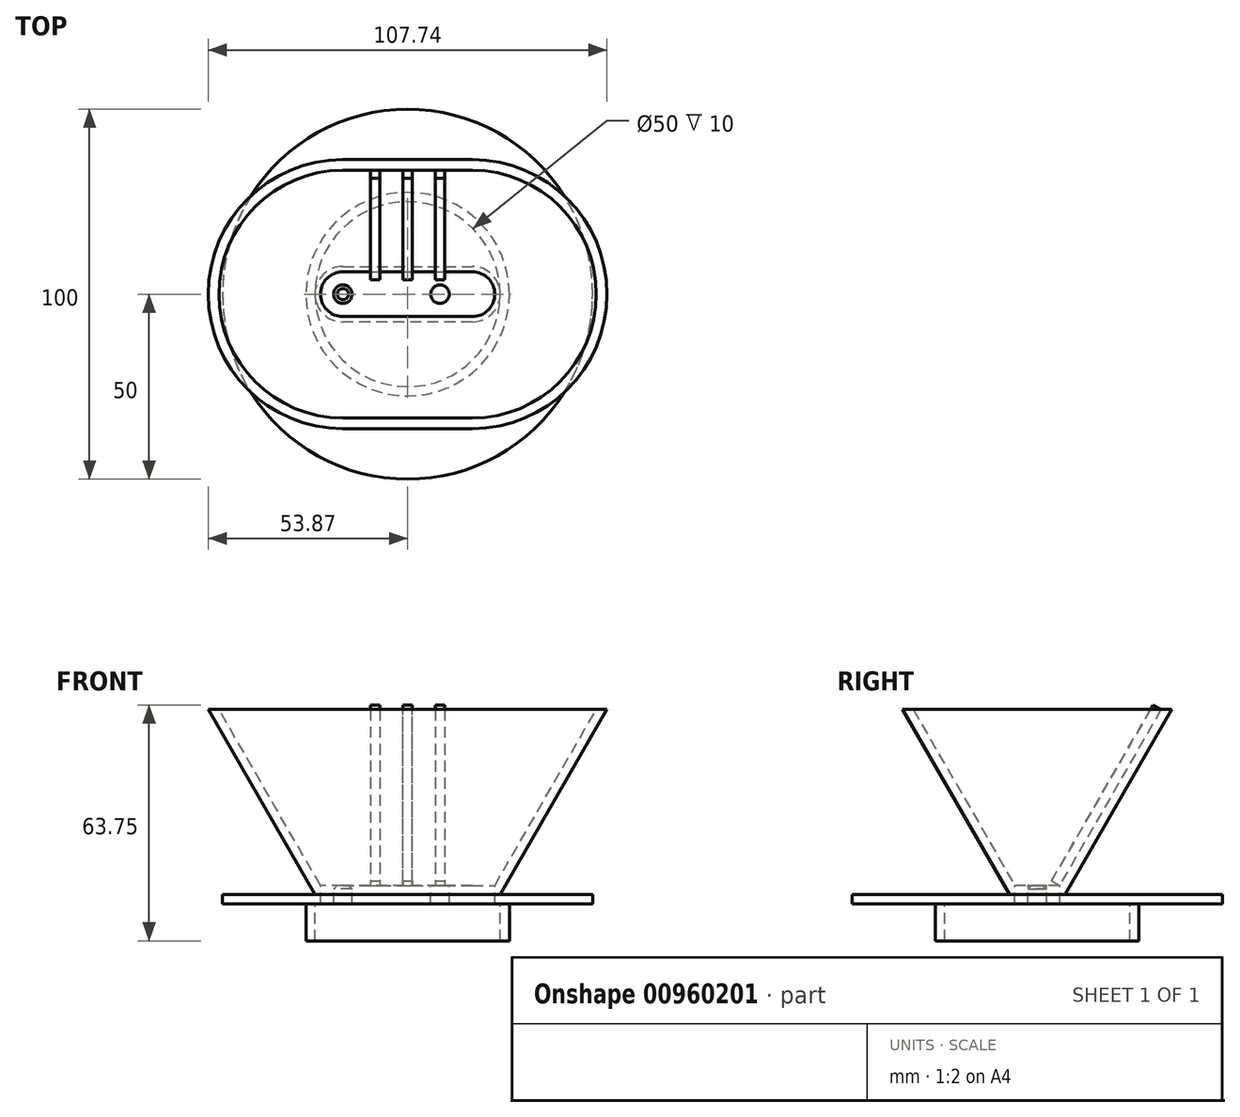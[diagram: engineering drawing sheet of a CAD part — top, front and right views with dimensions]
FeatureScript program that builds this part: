
annotation { "Feature Type Name" : "Feature", "Feature Type Description" : "" }
export const myFeature = defineFeature(function(context is Context, id is Id, definition is map)
    precondition{}
    {
        {
            var Q0;
            Q0=qCreatedBy(makeId("Top.planeOp"),FACE);
            var sketch = newSketch(context, id + "F0", { "sketchPlane" : qUnion([Q0])});
            skLineSegment(sketch, "E0.bottom", {"start": v(17.5, 7.5) * mm, "end": v(-17.5, 7.5) * mm});
            skLineSegment(sketch, "E0.top", {"start": v(17.5, -7.5) * mm, "end": v(-17.5, -7.5) * mm});
            skLineSegment(sketch, "E0.left", {"start": v(25, 0) * mm, "end": v(25, 0) * mm});
            skLineSegment(sketch, "E0.right", {"start": v(-25, 0) * mm, "end": v(-25, 0) * mm});
            skPoint(sketch, "E0.middle", {"position": v(0, 0) * mm});
            skPoint(sketch, "E1.visualSharp", {"position": v(-25, 7.5) * mm});
            skArc(sketch, "E1.filletArc", {"start": v(-17.5, 7.5) * mm, "mid": v(-22.8, 5.3) * mm, "end": v(-25, 0) * mm});
            skPoint(sketch, "E2.visualSharp", {"position": v(-25, -7.5) * mm});
            skArc(sketch, "E2.filletArc", {"start": v(-25, 0) * mm, "mid": v(-22.8, -5.3) * mm, "end": v(-17.5, -7.5) * mm});
            skPoint(sketch, "E3.visualSharp", {"position": v(25, -7.5) * mm});
            skArc(sketch, "E3.filletArc", {"start": v(17.5, -7.5) * mm, "mid": v(22.8, -5.3) * mm, "end": v(25, 0) * mm});
            skPoint(sketch, "E4.visualSharp", {"position": v(25, 7.5) * mm});
            skArc(sketch, "E4.filletArc", {"start": v(25, 0) * mm, "mid": v(22.8, 5.3) * mm, "end": v(17.5, 7.5) * mm});
            skSolve(sketch);
        }
        {
            var Q0;
            Q0=makeQuery(id+"F0.imprint","IMPRINT",FACE,{"disambiguationData":[TD([[makeQuery(id+"F0.imprint","IMPRINT",EDGE,{"derivedFrom":sQuery(id+"F0.wireOp",EDGE,"E0.bottom")}),1.0]])]});
            extrude(context, id + "F1", {"entities" : qUnion([Q0]), "depth" : 50 * mm, "offsetDistance" : 25 * mm, "hasDraft" : true, "draftAngle" : 30 * degree});
        }
        {
            var Q0;
            Q0=makeQuery(id+"F1.opExtrude","CAP_FACE",FACE,{"disambiguationData":[OSD([sQuery(id+"F0.wireOp",EDGE,"E0.bottom"),sQuery(id+"F0.wireOp",EDGE,"E0.top"),sQuery(id+"F0.wireOp",EDGE,"E0.left"),sQuery(id+"F0.wireOp",EDGE,"E0.right"),sQuery(id+"F0.wireOp",EDGE,"E1.filletArc"),sQuery(id+"F0.wireOp",EDGE,"E2.filletArc"),sQuery(id+"F0.wireOp",EDGE,"E3.filletArc"),sQuery(id+"F0.wireOp",EDGE,"E4.filletArc")])],"isStart":false});
            shell(context, id + "F2", {"entities" : qUnion([Q0]), "thickness" : 2.5 * mm});
        }
        {
            var Q0;
            Q0=makeQuery(id+"F1.opExtrude","CAP_FACE",FACE,{"disambiguationData":[OSD([sQuery(id+"F0.wireOp",EDGE,"E0.bottom"),sQuery(id+"F0.wireOp",EDGE,"E0.top"),sQuery(id+"F0.wireOp",EDGE,"E1.filletArc"),sQuery(id+"F0.wireOp",EDGE,"E2.filletArc"),sQuery(id+"F0.wireOp",EDGE,"E3.filletArc"),sQuery(id+"F0.wireOp",EDGE,"E4.filletArc")])],"isStart":true});
            var sketch = newSketch(context, id + "F3", { "sketchPlane" : qUnion([Q0])});
            skCircle(sketch, "E5", {"center": v(0, 0) * mm, "radius": 50 * mm});
            skSolve(sketch);
        }
        {
            var Q0;
            Q0 = qSketchRegion(id + "F3", true);
            extrude(context, id + "F4", {"entities" : qUnion([Q0]), "operationType" : NewBodyOperationType.ADD, "depth" : 2.5 * mm, "offsetDistance" : 25 * mm});
        }
        {
            var Q0;
            Q0=makeQuery(id+"F4.opExtrude","CAP_FACE",FACE,{"disambiguationData":[OSD([sQuery(id+"F3.wireOp",EDGE,"E5")])],"isStart":false});
            var sketch = newSketch(context, id + "F5", { "sketchPlane" : qUnion([Q0])});
            skCircle(sketch, "E6", {"center": v(0, 0) * mm, "radius": 25 * mm});
            skCircle(sketch, "E7", {"center": v(0, 0) * mm, "radius": 27.5 * mm});
            skSolve(sketch);
        }
        {
            var Q0;
            Q0=makeQuery(id+"F5.imprint","IMPRINT",FACE,{"disambiguationData":[TD([[makeQuery(id+"F5.imprint","IMPRINT",EDGE,{"derivedFrom":sQuery(id+"F5.wireOp",EDGE,"E6")}),-1.0]])]});
            extrude(context, id + "F6", {"entities" : qUnion([Q0]), "operationType" : NewBodyOperationType.ADD, "depth" : 10 * mm, "offsetDistance" : 25 * mm});
        }
        {
            var Q0;
            Q0=makeQuery(id+"F2.opShell","OFFSET_FACE",FACE,{"disambiguationData":[OSD([sQuery(id+"F0.wireOp",EDGE,"E0.bottom"),sQuery(id+"F0.wireOp",EDGE,"E0.top"),sQuery(id+"F0.wireOp",EDGE,"E1.filletArc"),sQuery(id+"F0.wireOp",EDGE,"E2.filletArc"),sQuery(id+"F0.wireOp",EDGE,"E3.filletArc"),sQuery(id+"F0.wireOp",EDGE,"E4.filletArc")])]});
            var sketch = newSketch(context, id + "F7", { "sketchPlane" : qUnion([Q0])});
            skLineSegment(sketch, "E8", {"start": v(-30.38, 0) * mm, "end": v(44.27, 0) * mm, "construction": true});
            skLineSegment(sketch, "E9", {"start": v(0, 19.87) * mm, "end": v(0, -23.96) * mm, "construction": true});
            skCircle(sketch, "E10", {"center": v(0, 0) * mm, "radius": 2.5 * mm});
            skCircle(sketch, "E11", {"center": v(17.5, 0) * mm, "radius": 2.5 * mm});
            skCircle(sketch, "E12.MirrorC", {"center": v(-17.5, 0) * mm, "radius": 2.5 * mm});
            skCircle(sketch, "E13", {"center": v(-8.75, 0) * mm, "radius": 2.5 * mm});
            skCircle(sketch, "E14.MirrorC", {"center": v(8.75, 0) * mm, "radius": 2.5 * mm});
            skSolve(sketch);
        }
        {
            var Q0;
            Q0=makeQuery(id+"F7.imprint","IMPRINT",FACE,{"disambiguationData":[TD([[makeQuery(id+"F7.imprint","IMPRINT",EDGE,{"derivedFrom":sQuery(id+"F7.wireOp",EDGE,"E12.MirrorC")}),-1.0]])]});
            var Q1;
            Q1=makeQuery(id+"F7.imprint","IMPRINT",FACE,{"disambiguationData":[TD([[makeQuery(id+"F7.imprint","IMPRINT",EDGE,{"derivedFrom":sQuery(id+"F7.wireOp",EDGE,"E13")}),1.0]])]});
            var Q2;
            Q2=makeQuery(id+"F7.imprint","IMPRINT",FACE,{"disambiguationData":[TD([[makeQuery(id+"F7.imprint","IMPRINT",EDGE,{"derivedFrom":sQuery(id+"F7.wireOp",EDGE,"E10")}),1.0]])]});
            var Q3;
            Q3=makeQuery(id+"F7.imprint","IMPRINT",FACE,{"disambiguationData":[TD([[makeQuery(id+"F7.imprint","IMPRINT",EDGE,{"derivedFrom":sQuery(id+"F7.wireOp",EDGE,"E14.MirrorC")}),-1.0]])]});
            var Q4;
            Q4=makeQuery(id+"F7.imprint","IMPRINT",FACE,{"disambiguationData":[TD([[makeQuery(id+"F7.imprint","IMPRINT",EDGE,{"derivedFrom":sQuery(id+"F7.wireOp",EDGE,"E11")}),1.0]])]});
            extrude(context, id + "F8", {"entities" : qUnion([Q0, Q1, Q2, Q3, Q4]), "operationType" : NewBodyOperationType.REMOVE, "endBound" : BoundingType.THROUGH_ALL, "oppositeDirection" : true, "depth" : 25 * mm, "offsetDistance" : 25 * mm});
        }
        {
            var Q0;
            Q0=makeQuery(id+"F8.boolean.opBoolean","COPY",EDGE,{"derivedFrom":makeQuery(id+"F8.opExtrude","CAP_EDGE",EDGE,{"disambiguationData":[OSD([sQuery(id+"F7.wireOp",EDGE,"E12.MirrorC")])],"isStart":true})});
            var Q1;
            Q1=makeQuery(id+"F8.boolean.opBoolean","COPY",EDGE,{"derivedFrom":makeQuery(id+"F8.opExtrude","CAP_EDGE",EDGE,{"disambiguationData":[OSD([sQuery(id+"F7.wireOp",EDGE,"E13")])],"isStart":true})});
            var Q2;
            Q2=makeQuery(id+"F8.boolean.opBoolean","COPY",EDGE,{"derivedFrom":makeQuery(id+"F8.opExtrude","CAP_EDGE",EDGE,{"disambiguationData":[OSD([sQuery(id+"F7.wireOp",EDGE,"E10")])],"isStart":true})});
            var Q3;
            Q3=makeQuery(id+"F8.boolean.opBoolean","COPY",EDGE,{"derivedFrom":makeQuery(id+"F8.opExtrude","CAP_EDGE",EDGE,{"disambiguationData":[OSD([sQuery(id+"F7.wireOp",EDGE,"E14.MirrorC")])],"isStart":true})});
            var Q4;
            Q4=makeQuery(id+"F8.boolean.opBoolean","COPY",EDGE,{"derivedFrom":makeQuery(id+"F8.opExtrude","CAP_EDGE",EDGE,{"disambiguationData":[OSD([sQuery(id+"F7.wireOp",EDGE,"E11")])],"isStart":true})});
            chamfer(context, id + "F9", {"entities" : qUnion([Q0, Q1, Q2, Q3, Q4]), "width" : 1 * mm, "tangentPropagation" : true});
        }
        {
            var Q0;
            Q0=makeQuery(id+"F2.opShell","OFFSET_FACE",FACE,{"disambiguationData":[OSD([sQuery(id+"F0.wireOp",EDGE,"E0.bottom")])]});
            var sketch = newSketch(context, id + "F10", { "sketchPlane" : qUnion([Q0])});
            skLineSegment(sketch, "E15.bottom", {"start": v(-1.25, 5.2) * mm, "end": v(1.25, 5.2) * mm});
            skLineSegment(sketch, "E15.top", {"start": v(-1.25, 60.04) * mm, "end": v(1.25, 60.04) * mm});
            skLineSegment(sketch, "E15.left", {"start": v(-1.25, 5.2) * mm, "end": v(-1.25, 60.04) * mm});
            skLineSegment(sketch, "E15.right", {"start": v(1.25, 5.2) * mm, "end": v(1.25, 60.04) * mm});
            skLineSegment(sketch, "E16", {"start": v(0, 5.2) * mm, "end": v(0, 60.04) * mm, "construction": true});
            skLineSegment(sketch, "E17.bottom", {"start": v(-10, 60.04) * mm, "end": v(-7.5, 60.04) * mm});
            skLineSegment(sketch, "E17.top", {"start": v(-10, 5.2) * mm, "end": v(-7.5, 5.2) * mm});
            skLineSegment(sketch, "E17.left", {"start": v(-10, 60.04) * mm, "end": v(-10, 5.2) * mm});
            skLineSegment(sketch, "E17.right", {"start": v(-7.5, 60.04) * mm, "end": v(-7.5, 5.2) * mm});
            skLineSegment(sketch, "E18.MirrorCS", {"start": v(7.5, 60.04) * mm, "end": v(7.5, 5.2) * mm});
            skLineSegment(sketch, "E19.MirrorCS", {"start": v(10, 60.04) * mm, "end": v(10, 5.2) * mm});
            skLineSegment(sketch, "E20.MirrorCS", {"start": v(10, 60.04) * mm, "end": v(7.5, 60.04) * mm});
            skLineSegment(sketch, "E21.MirrorCS", {"start": v(10, 5.2) * mm, "end": v(7.5, 5.2) * mm});
            skSolve(sketch);
        }
        {
            var Q0;
            Q0 = qSketchRegion(id + "F10", true);
            extrude(context, id + "F11", {"entities" : qUnion([Q0]), "operationType" : NewBodyOperationType.ADD, "depth" : 2.5 * mm, "offsetDistance" : 25 * mm});
        }
    });
